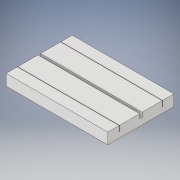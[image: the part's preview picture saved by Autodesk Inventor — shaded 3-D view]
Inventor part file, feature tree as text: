
AUTODESK INVENTOR PART (.ipt)
format: ipt  version: 2018 (Build 220112000, 112)  size: 114,688 bytes
history: native  units: in
note: dims shown in document units (in); Inventor stores cm internally (conversion verified against a paired STEP export)
features: extrude x2, sketch x2
ambient origin geometry x8: Origin, YZ Plane, XZ Plane, XY Plane, X Axis, Y Axis, Z Axis, Center Point
bodies: Solid1 (feature_tree)
feature tree (4):
  extrude  "Extrusion1"  Depth=2.126in
  extrude  "Extrusion2"  Depth=0.0787in
  sketch  "Sketch1"  dims[d0=3.2677in d1=2.126in]
  sketch  "Sketch2"  dims[d2=0.3543in d3=0.0in d4=0.689in d5=0.0098in d6=0.0787in d7=0.2769in d8=4.2918in d9=0.0in]
